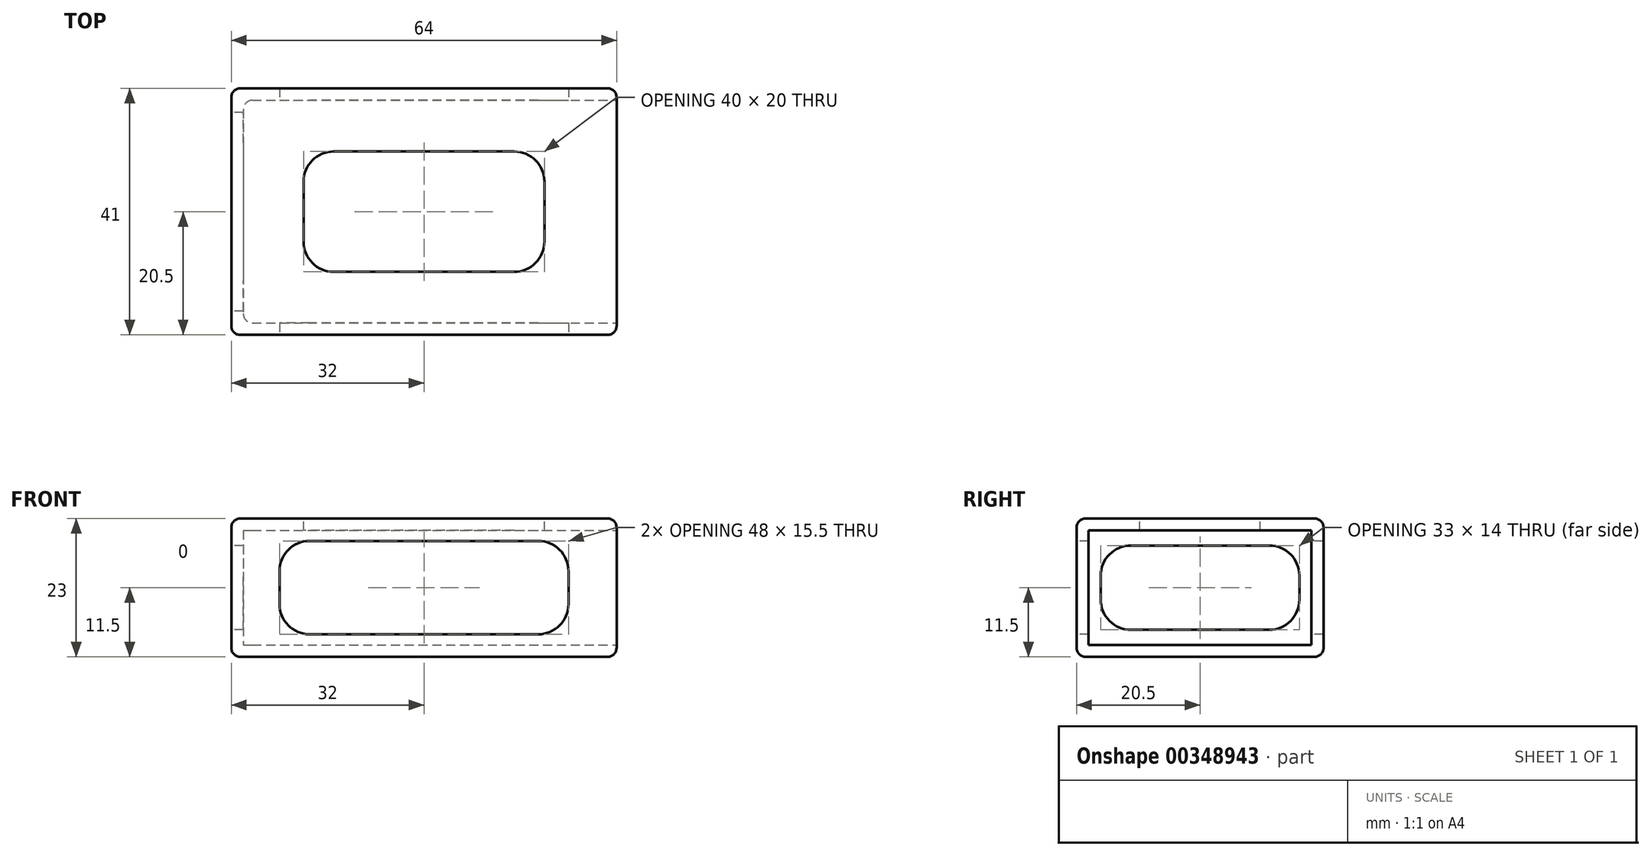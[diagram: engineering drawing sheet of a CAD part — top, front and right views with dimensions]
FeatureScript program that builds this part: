
annotation { "Feature Type Name" : "Feature", "Feature Type Description" : "" }
export const myFeature = defineFeature(function(context is Context, id is Id, definition is map)
    precondition{}
    {
        {
            var Q0;
            Q0=qCreatedBy(makeId("Top.planeOp"),FACE);
            var sketch = newSketch(context, id + "F0", { "sketchPlane" : qUnion([Q0])});
            skLineSegment(sketch, "E0.bottom", {"start": v(32, 20.5) * mm, "end": v(-32, 20.5) * mm});
            skLineSegment(sketch, "E0.top", {"start": v(32, -20.5) * mm, "end": v(-32, -20.5) * mm});
            skLineSegment(sketch, "E0.left", {"start": v(32, 20.5) * mm, "end": v(32, -20.5) * mm});
            skLineSegment(sketch, "E0.right", {"start": v(-32, 20.5) * mm, "end": v(-32, -20.5) * mm});
            skPoint(sketch, "E0.middle", {"position": v(0, 0) * mm});
            skSolve(sketch);
        }
        {
            var Q0;
            Q0=makeQuery(id+"F0.imprint","IMPRINT",FACE,{"disambiguationData":[TD([[makeQuery(id+"F0.imprint","IMPRINT",EDGE,{"derivedFrom":sQuery(id+"F0.wireOp",EDGE,"E0.bottom")}),1.0]])]});
            extrude(context, id + "F1", {"entities" : qUnion([Q0]), "depth" : 11.5 * mm});
        }
        {
            var Q0;
            Q0=makeQuery(id+"F1.opExtrude","CAP_EDGE",EDGE,{"disambiguationData":[OSD([sQuery(id+"F0.wireOp",EDGE,"E0.right")])],"isStart":false});
            var Q1;
            Q1=makeQuery(id+"F1.opExtrude","CAP_EDGE",EDGE,{"disambiguationData":[OSD([sQuery(id+"F0.wireOp",EDGE,"E0.top")])],"isStart":false});
            var Q2;
            Q2=makeQuery(id+"F1.opExtrude","CAP_EDGE",EDGE,{"disambiguationData":[OSD([sQuery(id+"F0.wireOp",EDGE,"E0.left")])],"isStart":false});
            var Q3;
            Q3=makeQuery(id+"F1.opExtrude","CAP_EDGE",EDGE,{"disambiguationData":[OSD([sQuery(id+"F0.wireOp",EDGE,"E0.bottom")])],"isStart":false});
            var Q4;
            Q4=makeQuery(id+"F1.opExtrude","SWEPT_EDGE",EDGE,{"disambiguationData":[OSD([sQuery(id+"F0.wireOp",EDGE,"E0.top"),sQuery(id+"F0.wireOp",EDGE,"E0.left")])]});
            var Q5;
            Q5=makeQuery(id+"F1.opExtrude","SWEPT_EDGE",EDGE,{"disambiguationData":[OSD([sQuery(id+"F0.wireOp",EDGE,"E0.bottom"),sQuery(id+"F0.wireOp",EDGE,"E0.left")])]});
            var Q6;
            Q6=makeQuery(id+"F1.opExtrude","SWEPT_EDGE",EDGE,{"disambiguationData":[OSD([sQuery(id+"F0.wireOp",EDGE,"E0.top"),sQuery(id+"F0.wireOp",EDGE,"E0.right")])]});
            var Q7;
            Q7=makeQuery(id+"F1.opExtrude","SWEPT_EDGE",EDGE,{"disambiguationData":[OSD([sQuery(id+"F0.wireOp",EDGE,"E0.bottom"),sQuery(id+"F0.wireOp",EDGE,"E0.right")])]});
            fillet(context, id + "F2", {"entities" : qUnion([Q0, Q1, Q2, Q3, Q4, Q5, Q6, Q7]), "radius" : 1.5 * mm, "tangentPropagation" : true, "allowEdgeOverflow" : false});
        }
        {
            var Q0;
            Q0=makeQuery(id+"F1.opExtrude","CAP_FACE",FACE,{"disambiguationData":[OSD([sQuery(id+"F0.wireOp",EDGE,"E0.bottom"),sQuery(id+"F0.wireOp",EDGE,"E0.top"),sQuery(id+"F0.wireOp",EDGE,"E0.left"),sQuery(id+"F0.wireOp",EDGE,"E0.right")])],"isStart":true});
            shell(context, id + "F3", {"entities" : qUnion([Q0]), "thickness" : 2 * mm});
        }
        {
            var Q0;
            Q0=makeQuery(id+"F3.opShell","OFFSET_EDGE",EDGE,{"disambiguationData":[OSD([sQuery(id+"F0.wireOp",EDGE,"E0.bottom"),sQuery(id+"F0.wireOp",EDGE,"E0.right")])]});
            var Q1;
            Q1=makeQuery(id+"F3.opShell","OFFSET_EDGE",EDGE,{"disambiguationData":[OSD([sQuery(id+"F0.wireOp",EDGE,"E0.top"),sQuery(id+"F0.wireOp",EDGE,"E0.right")])]});
            fillet(context, id + "F4", {"entities" : qUnion([Q0, Q1]), "radius" : 1.5 * mm, "tangentPropagation" : true, "allowEdgeOverflow" : false});
        }
        {
            var Q0;
            Q0=makeQuery(id+"F1.opExtrude","SWEPT_BODY",BODY,{"disambiguationData":[OSD([sQuery(id+"F0.wireOp",EDGE,"E0.bottom"),sQuery(id+"F0.wireOp",EDGE,"E0.top"),sQuery(id+"F0.wireOp",EDGE,"E0.left"),sQuery(id+"F0.wireOp",EDGE,"E0.right")])]});
            var Q1;
            Q1=qCreatedBy(makeId("Top.planeOp"),FACE);
            mirror(context, id + "F5", {"operationType" : NewBodyOperationType.ADD, "entities" : qUnion([Q0]), "mirrorPlane" : qUnion([Q1])});
        }
        {
            var Q0;
            {var subQ0=makeQuery(id+"F1.opExtrude","SWEPT_FACE",FACE,{"disambiguationData":[OSD([sQuery(id+"F0.wireOp",EDGE,"E0.top")])]});Q0=makeQuery(id+"F5.boolean.opBoolean","MERGE",FACE,{"derivedFrom":[subQ0,makeQuery(id+"F5.opPattern","COPY",FACE,{"derivedFrom":subQ0,"instanceName":"1"})]});}
            var sketch = newSketch(context, id + "F6", { "sketchPlane" : qUnion([Q0])});
            skLineSegment(sketch, "E1.bottom", {"start": v(24, -7.75) * mm, "end": v(-24, -7.75) * mm});
            skLineSegment(sketch, "E1.top", {"start": v(24, 7.75) * mm, "end": v(-24, 7.75) * mm});
            skLineSegment(sketch, "E1.left", {"start": v(24, -7.75) * mm, "end": v(24, 7.75) * mm});
            skLineSegment(sketch, "E1.right", {"start": v(-24, -7.75) * mm, "end": v(-24, 7.75) * mm});
            skPoint(sketch, "E1.middle", {"position": v(0, 0) * mm});
            skSolve(sketch);
        }
        {
            var Q0;
            Q0=makeQuery(id+"F6.imprint","IMPRINT",FACE,{"disambiguationData":[TD([[makeQuery(id+"F6.imprint","IMPRINT",EDGE,{"derivedFrom":sQuery(id+"F6.wireOp",EDGE,"E1.bottom")}),-1.0]])]});
            extrude(context, id + "F7", {"entities" : qUnion([Q0]), "operationType" : NewBodyOperationType.REMOVE, "endBound" : BoundingType.THROUGH_ALL, "oppositeDirection" : true, "depth" : 5 * mm});
        }
        {
            var Q0;
            {var subQ0=makeQuery(id+"F1.opExtrude","SWEPT_FACE",FACE,{"disambiguationData":[OSD([sQuery(id+"F0.wireOp",EDGE,"E0.right")])]});Q0=makeQuery(id+"F5.boolean.opBoolean","MERGE",FACE,{"derivedFrom":[subQ0,makeQuery(id+"F5.opPattern","COPY",FACE,{"derivedFrom":subQ0,"instanceName":"1"})]});}
            var sketch = newSketch(context, id + "F8", { "sketchPlane" : qUnion([Q0])});
            skLineSegment(sketch, "E2.bottom", {"start": v(16.5, 7) * mm, "end": v(-16.5, 7) * mm});
            skLineSegment(sketch, "E2.top", {"start": v(16.5, -7) * mm, "end": v(-16.5, -7) * mm});
            skLineSegment(sketch, "E2.left", {"start": v(16.5, 7) * mm, "end": v(16.5, -7) * mm});
            skLineSegment(sketch, "E2.right", {"start": v(-16.5, 7) * mm, "end": v(-16.5, -7) * mm});
            skPoint(sketch, "E2.middle", {"position": v(0, 0) * mm});
            skSolve(sketch);
        }
        {
            var Q0;
            Q0=makeQuery(id+"F8.imprint","IMPRINT",FACE,{"disambiguationData":[TD([[makeQuery(id+"F8.imprint","IMPRINT",EDGE,{"derivedFrom":sQuery(id+"F8.wireOp",EDGE,"E2.bottom")}),1.0]])]});
            extrude(context, id + "F9", {"entities" : qUnion([Q0]), "operationType" : NewBodyOperationType.REMOVE, "oppositeDirection" : true, "depth" : 5 * mm});
        }
        {
            var Q0;
            {var subQ0=sQuery(id+"F0.wireOp",EDGE,"E0.left");var subQ2=makeQuery(id+"F1.opExtrude","SWEPT_FACE",FACE,{"disambiguationData":[OSD([subQ0])]});var subQ3=sQuery(id+"F8.wireOp",EDGE,"E2.right");var subQ4=sQuery(id+"F8.wireOp",EDGE,"E2.top");Q0=makeQuery(id+"F9.boolean.opBoolean","COPY",EDGE,{"disambiguationData":[TD([subQ2])],"derivedFrom":makeQuery(id+"F9.opExtrude","SWEPT_EDGE",EDGE,{"disambiguationData":[OSD([subQ4,subQ3])]})});}
            var Q1;
            {var subQ0=sQuery(id+"F0.wireOp",EDGE,"E0.right");var subQ2=makeQuery(id+"F1.opExtrude","SWEPT_FACE",FACE,{"disambiguationData":[OSD([subQ0])]});var subQ3=sQuery(id+"F8.wireOp",EDGE,"E2.top");var subQ4=sQuery(id+"F8.wireOp",EDGE,"E2.right");Q1=makeQuery(id+"F9.boolean.opBoolean","COPY",EDGE,{"disambiguationData":[TD([subQ2])],"derivedFrom":makeQuery(id+"F9.opExtrude","SWEPT_EDGE",EDGE,{"disambiguationData":[OSD([subQ3,subQ4])]})});}
            var Q2;
            {var subQ0=sQuery(id+"F0.wireOp",EDGE,"E0.left");var subQ2=makeQuery(id+"F1.opExtrude","SWEPT_FACE",FACE,{"disambiguationData":[OSD([subQ0])]});var subQ3=sQuery(id+"F8.wireOp",EDGE,"E2.top");var subQ4=sQuery(id+"F8.wireOp",EDGE,"E2.left");Q2=makeQuery(id+"F9.boolean.opBoolean","COPY",EDGE,{"disambiguationData":[TD([subQ2])],"derivedFrom":makeQuery(id+"F9.opExtrude","SWEPT_EDGE",EDGE,{"disambiguationData":[OSD([subQ3,subQ4])]})});}
            var Q3;
            {var subQ0=sQuery(id+"F0.wireOp",EDGE,"E0.right");var subQ2=makeQuery(id+"F1.opExtrude","SWEPT_FACE",FACE,{"disambiguationData":[OSD([subQ0])]});var subQ3=sQuery(id+"F8.wireOp",EDGE,"E2.top");var subQ4=sQuery(id+"F8.wireOp",EDGE,"E2.left");Q3=makeQuery(id+"F9.boolean.opBoolean","COPY",EDGE,{"disambiguationData":[TD([subQ2])],"derivedFrom":makeQuery(id+"F9.opExtrude","SWEPT_EDGE",EDGE,{"disambiguationData":[OSD([subQ3,subQ4])]})});}
            var Q4;
            {var subQ0=sQuery(id+"F0.wireOp",EDGE,"E0.left");var subQ2=makeQuery(id+"F1.opExtrude","SWEPT_FACE",FACE,{"disambiguationData":[OSD([subQ0])]});var subQ3=sQuery(id+"F8.wireOp",EDGE,"E2.right");var subQ4=sQuery(id+"F8.wireOp",EDGE,"E2.bottom");Q4=makeQuery(id+"F9.boolean.opBoolean","COPY",EDGE,{"disambiguationData":[TD([subQ2])],"derivedFrom":makeQuery(id+"F9.opExtrude","SWEPT_EDGE",EDGE,{"disambiguationData":[OSD([subQ4,subQ3])]})});}
            var Q5;
            {var subQ0=sQuery(id+"F0.wireOp",EDGE,"E0.right");var subQ2=makeQuery(id+"F1.opExtrude","SWEPT_FACE",FACE,{"disambiguationData":[OSD([subQ0])]});var subQ3=sQuery(id+"F8.wireOp",EDGE,"E2.bottom");var subQ4=sQuery(id+"F8.wireOp",EDGE,"E2.right");Q5=makeQuery(id+"F9.boolean.opBoolean","COPY",EDGE,{"disambiguationData":[TD([subQ2])],"derivedFrom":makeQuery(id+"F9.opExtrude","SWEPT_EDGE",EDGE,{"disambiguationData":[OSD([subQ3,subQ4])]})});}
            var Q6;
            {var subQ0=sQuery(id+"F0.wireOp",EDGE,"E0.right");var subQ2=sQuery(id+"F8.wireOp",EDGE,"E2.bottom");var subQ3=makeQuery(id+"F1.opExtrude","SWEPT_FACE",FACE,{"disambiguationData":[OSD([subQ0])]});var subQ4=sQuery(id+"F8.wireOp",EDGE,"E2.left");Q6=makeQuery(id+"F9.boolean.opBoolean","COPY",EDGE,{"disambiguationData":[TD([subQ3])],"derivedFrom":makeQuery(id+"F9.opExtrude","SWEPT_EDGE",EDGE,{"disambiguationData":[OSD([subQ2,subQ4])]})});}
            var Q7;
            {var subQ0=sQuery(id+"F0.wireOp",EDGE,"E0.left");var subQ2=makeQuery(id+"F1.opExtrude","SWEPT_FACE",FACE,{"disambiguationData":[OSD([subQ0])]});var subQ3=sQuery(id+"F8.wireOp",EDGE,"E2.bottom");var subQ4=sQuery(id+"F8.wireOp",EDGE,"E2.left");Q7=makeQuery(id+"F9.boolean.opBoolean","COPY",EDGE,{"disambiguationData":[TD([subQ2])],"derivedFrom":makeQuery(id+"F9.opExtrude","SWEPT_EDGE",EDGE,{"disambiguationData":[OSD([subQ3,subQ4])]})});}
            fillet(context, id + "F10", {"entities" : qUnion([Q0, Q1, Q2, Q3, Q4, Q5, Q6, Q7]), "radius" : 5 * mm, "tangentPropagation" : true, "allowEdgeOverflow" : false});
        }
        {
            var Q0;
            {var subQ0=sQuery(id+"F0.wireOp",EDGE,"E0.top");var subQ2=makeQuery(id+"F1.opExtrude","SWEPT_FACE",FACE,{"disambiguationData":[OSD([subQ0])]});var subQ3=sQuery(id+"F6.wireOp",EDGE,"E1.top");var subQ4=sQuery(id+"F6.wireOp",EDGE,"E1.right");Q0=makeQuery(id+"F7.boolean.opBoolean","COPY",EDGE,{"disambiguationData":[TD([subQ2])],"derivedFrom":makeQuery(id+"F7.opExtrude","SWEPT_EDGE",EDGE,{"disambiguationData":[OSD([subQ3,subQ4])]})});}
            var Q1;
            {var subQ0=sQuery(id+"F0.wireOp",EDGE,"E0.top");var subQ2=makeQuery(id+"F1.opExtrude","SWEPT_FACE",FACE,{"disambiguationData":[OSD([subQ0])]});var subQ3=sQuery(id+"F6.wireOp",EDGE,"E1.left");var subQ4=sQuery(id+"F6.wireOp",EDGE,"E1.top");Q1=makeQuery(id+"F7.boolean.opBoolean","COPY",EDGE,{"disambiguationData":[TD([subQ2])],"derivedFrom":makeQuery(id+"F7.opExtrude","SWEPT_EDGE",EDGE,{"disambiguationData":[OSD([subQ4,subQ3])]})});}
            var Q2;
            {var subQ0=sQuery(id+"F0.wireOp",EDGE,"E0.top");var subQ2=sQuery(id+"F6.wireOp",EDGE,"E1.bottom");var subQ3=makeQuery(id+"F1.opExtrude","SWEPT_FACE",FACE,{"disambiguationData":[OSD([subQ0])]});var subQ4=sQuery(id+"F6.wireOp",EDGE,"E1.right");Q2=makeQuery(id+"F7.boolean.opBoolean","COPY",EDGE,{"disambiguationData":[TD([subQ3])],"derivedFrom":makeQuery(id+"F7.opExtrude","SWEPT_EDGE",EDGE,{"disambiguationData":[OSD([subQ2,subQ4])]})});}
            var Q3;
            {var subQ0=sQuery(id+"F0.wireOp",EDGE,"E0.top");var subQ2=sQuery(id+"F6.wireOp",EDGE,"E1.bottom");var subQ3=makeQuery(id+"F1.opExtrude","SWEPT_FACE",FACE,{"disambiguationData":[OSD([subQ0])]});var subQ4=sQuery(id+"F6.wireOp",EDGE,"E1.left");Q3=makeQuery(id+"F7.boolean.opBoolean","COPY",EDGE,{"disambiguationData":[TD([subQ3])],"derivedFrom":makeQuery(id+"F7.opExtrude","SWEPT_EDGE",EDGE,{"disambiguationData":[OSD([subQ2,subQ4])]})});}
            fillet(context, id + "F11", {"entities" : qUnion([Q0, Q1, Q2, Q3]), "radius" : 5 * mm, "tangentPropagation" : true, "allowEdgeOverflow" : false});
        }
        {
            var Q0;
            {var subQ0=sQuery(id+"F0.wireOp",EDGE,"E0.bottom");var subQ1=makeQuery(id+"F1.opExtrude","SWEPT_FACE",FACE,{"disambiguationData":[OSD([subQ0])]});var subQ3=sQuery(id+"F6.wireOp",EDGE,"E1.top");var subQ4=sQuery(id+"F6.wireOp",EDGE,"E1.left");Q0=makeQuery(id+"F7.boolean.opBoolean","COPY",EDGE,{"disambiguationData":[TD([subQ1])],"derivedFrom":makeQuery(id+"F7.opExtrude","SWEPT_EDGE",EDGE,{"disambiguationData":[OSD([subQ3,subQ4])]})});}
            var Q1;
            {var subQ0=sQuery(id+"F0.wireOp",EDGE,"E0.bottom");var subQ1=makeQuery(id+"F1.opExtrude","SWEPT_FACE",FACE,{"disambiguationData":[OSD([subQ0])]});var subQ3=sQuery(id+"F6.wireOp",EDGE,"E1.bottom");var subQ4=sQuery(id+"F6.wireOp",EDGE,"E1.left");Q1=makeQuery(id+"F7.boolean.opBoolean","COPY",EDGE,{"disambiguationData":[TD([subQ1])],"derivedFrom":makeQuery(id+"F7.opExtrude","SWEPT_EDGE",EDGE,{"disambiguationData":[OSD([subQ3,subQ4])]})});}
            var Q2;
            {var subQ0=sQuery(id+"F0.wireOp",EDGE,"E0.bottom");var subQ1=makeQuery(id+"F1.opExtrude","SWEPT_FACE",FACE,{"disambiguationData":[OSD([subQ0])]});var subQ3=sQuery(id+"F6.wireOp",EDGE,"E1.right");var subQ4=sQuery(id+"F6.wireOp",EDGE,"E1.bottom");Q2=makeQuery(id+"F7.boolean.opBoolean","COPY",EDGE,{"disambiguationData":[TD([subQ1])],"derivedFrom":makeQuery(id+"F7.opExtrude","SWEPT_EDGE",EDGE,{"disambiguationData":[OSD([subQ4,subQ3])]})});}
            var Q3;
            {var subQ0=sQuery(id+"F0.wireOp",EDGE,"E0.bottom");var subQ1=makeQuery(id+"F1.opExtrude","SWEPT_FACE",FACE,{"disambiguationData":[OSD([subQ0])]});var subQ3=sQuery(id+"F6.wireOp",EDGE,"E1.right");var subQ4=sQuery(id+"F6.wireOp",EDGE,"E1.top");Q3=makeQuery(id+"F7.boolean.opBoolean","COPY",EDGE,{"disambiguationData":[TD([subQ1])],"derivedFrom":makeQuery(id+"F7.opExtrude","SWEPT_EDGE",EDGE,{"disambiguationData":[OSD([subQ4,subQ3])]})});}
            fillet(context, id + "F12", {"entities" : qUnion([Q0, Q1, Q2, Q3]), "radius" : 5 * mm, "tangentPropagation" : true, "allowEdgeOverflow" : false});
        }
        {
            var Q0;
            Q0=makeQuery(id+"F1.opExtrude","CAP_FACE",FACE,{"disambiguationData":[OSD([sQuery(id+"F0.wireOp",EDGE,"E0.bottom"),sQuery(id+"F0.wireOp",EDGE,"E0.top"),sQuery(id+"F0.wireOp",EDGE,"E0.left"),sQuery(id+"F0.wireOp",EDGE,"E0.right")])],"isStart":false});
            var sketch = newSketch(context, id + "F13", { "sketchPlane" : qUnion([Q0])});
            skLineSegment(sketch, "E3.bottom", {"start": v(20, -10) * mm, "end": v(-20, -10) * mm});
            skLineSegment(sketch, "E3.top", {"start": v(20, 10) * mm, "end": v(-20, 10) * mm});
            skLineSegment(sketch, "E3.left", {"start": v(20, -10) * mm, "end": v(20, 10) * mm});
            skLineSegment(sketch, "E3.right", {"start": v(-20, -10) * mm, "end": v(-20, 10) * mm});
            skPoint(sketch, "E3.middle", {"position": v(0, 0) * mm});
            skSolve(sketch);
        }
        {
            var Q0;
            Q0=makeQuery(id+"F13.imprint","IMPRINT",FACE,{"disambiguationData":[TD([[makeQuery(id+"F13.imprint","IMPRINT",EDGE,{"derivedFrom":sQuery(id+"F13.wireOp",EDGE,"E3.bottom")}),-1.0]])]});
            extrude(context, id + "F14", {"entities" : qUnion([Q0]), "operationType" : NewBodyOperationType.REMOVE, "oppositeDirection" : true, "depth" : 5 * mm});
        }
        {
            var Q0;
            Q0=makeQuery(id+"F14.boolean.opBoolean","COPY",EDGE,{"derivedFrom":makeQuery(id+"F14.opExtrude","SWEPT_EDGE",EDGE,{"disambiguationData":[OSD([sQuery(id+"F13.wireOp",EDGE,"E3.top"),sQuery(id+"F13.wireOp",EDGE,"E3.right")])]})});
            var Q1;
            Q1=makeQuery(id+"F14.boolean.opBoolean","COPY",EDGE,{"derivedFrom":makeQuery(id+"F14.opExtrude","SWEPT_EDGE",EDGE,{"disambiguationData":[OSD([sQuery(id+"F13.wireOp",EDGE,"E3.bottom"),sQuery(id+"F13.wireOp",EDGE,"E3.right")])]})});
            var Q2;
            Q2=makeQuery(id+"F14.boolean.opBoolean","COPY",EDGE,{"derivedFrom":makeQuery(id+"F14.opExtrude","SWEPT_EDGE",EDGE,{"disambiguationData":[OSD([sQuery(id+"F13.wireOp",EDGE,"E3.bottom"),sQuery(id+"F13.wireOp",EDGE,"E3.left")])]})});
            var Q3;
            Q3=makeQuery(id+"F14.boolean.opBoolean","COPY",EDGE,{"derivedFrom":makeQuery(id+"F14.opExtrude","SWEPT_EDGE",EDGE,{"disambiguationData":[OSD([sQuery(id+"F13.wireOp",EDGE,"E3.top"),sQuery(id+"F13.wireOp",EDGE,"E3.left")])]})});
            fillet(context, id + "F15", {"entities" : qUnion([Q0, Q1, Q2, Q3]), "radius" : 5 * mm, "tangentPropagation" : true, "allowEdgeOverflow" : false});
        }
        {
            var Q0;
            {var subQ0=makeQuery(id+"F1.opExtrude","SWEPT_FACE",FACE,{"disambiguationData":[OSD([sQuery(id+"F0.wireOp",EDGE,"E0.left")])]});Q0=makeQuery(id+"F5.boolean.opBoolean","MERGE",FACE,{"derivedFrom":[subQ0,makeQuery(id+"F5.opPattern","COPY",FACE,{"derivedFrom":subQ0,"instanceName":"1"})]});}
            var sketch = newSketch(context, id + "F16", { "sketchPlane" : qUnion([Q0])});
            skLineSegment(sketch, "E4.bottom", {"start": v(18.5, -9.5) * mm, "end": v(-18.5, -9.5) * mm});
            skLineSegment(sketch, "E4.top", {"start": v(18.5, 9.5) * mm, "end": v(-18.5, 9.5) * mm});
            skLineSegment(sketch, "E4.left", {"start": v(18.5, -9.5) * mm, "end": v(18.5, 9.5) * mm});
            skLineSegment(sketch, "E4.right", {"start": v(-18.5, -9.5) * mm, "end": v(-18.5, 9.5) * mm});
            skPoint(sketch, "E4.middle", {"position": v(0, 0) * mm});
            skSolve(sketch);
        }
        {
            var Q0;
            Q0=makeQuery(id+"F16.imprint","IMPRINT",FACE,{"disambiguationData":[TD([[makeQuery(id+"F16.imprint","IMPRINT",EDGE,{"derivedFrom":sQuery(id+"F16.wireOp",EDGE,"E4.bottom")}),-1.0]])]});
            extrude(context, id + "F17", {"entities" : qUnion([Q0]), "operationType" : NewBodyOperationType.REMOVE, "oppositeDirection" : true, "depth" : 5 * mm});
        }
    });
